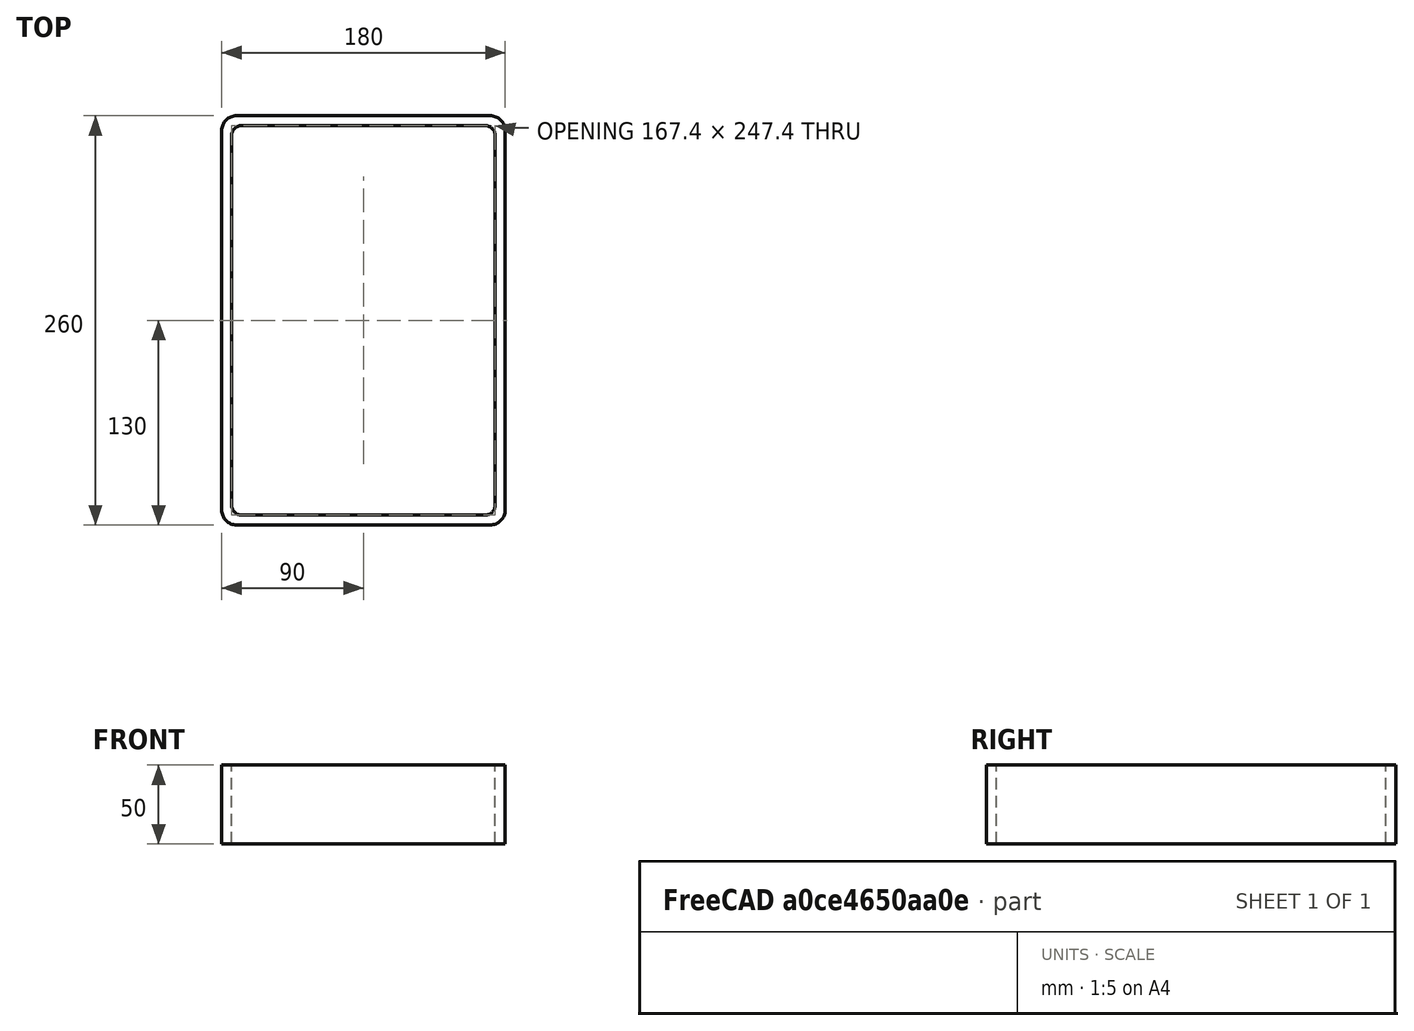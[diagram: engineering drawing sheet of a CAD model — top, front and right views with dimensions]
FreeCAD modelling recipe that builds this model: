
FCSTD DOCUMENT  (FreeCAD 0.15R4671 (Git))
Label: Rectangular hollow section 260x180x6.3 EN10219 S235JRH
License: All rights reserved
LicenseURL: http://en.wikipedia.org/wiki/All_rights_reserved
objects: Sketcher::SketchObject×1, Part::Extrusion×1
note: 2 computed .brp shape members not serialized (recipe doc carries the construction recipe); baked Part::Feature solids carry a one-line shape summary decoded from their .brp

FEATURE [Sketcher::SketchObject] Sketch
  sketch-geometry (16):
    g0: LineSegment StartX=-77.4 StartY=123.7 StartZ=0 EndX=77.4 EndY=123.7 EndZ=0
    g1: LineSegment StartX=83.7 StartY=117.4 StartZ=0 EndX=83.7 EndY=-117.4 EndZ=0
    g2: LineSegment StartX=77.4 StartY=-123.7 StartZ=0 EndX=-77.4 EndY=-123.7 EndZ=0
    g3: LineSegment StartX=-83.7 StartY=-117.4 StartZ=0 EndX=-83.7 EndY=117.4 EndZ=0
    g4: LineSegment StartX=-80.55 StartY=130 StartZ=0 EndX=80.55 EndY=130 EndZ=0
    g5: LineSegment StartX=90 StartY=120.55 StartZ=0 EndX=90 EndY=-120.55 EndZ=0
    g6: LineSegment StartX=80.55 StartY=-130 StartZ=0 EndX=-80.55 EndY=-130 EndZ=0
    g7: LineSegment StartX=-90 StartY=-120.55 StartZ=0 EndX=-90 EndY=120.55 EndZ=0
    g8: ArcOfCircle CenterX=-77.4 CenterY=117.4 CenterZ=0 NormalX=0 NormalY=0 NormalZ=1 Radius=6.3 StartAngle=1.5708 EndAngle=3.14159
    g9: ArcOfCircle CenterX=77.4 CenterY=117.4 CenterZ=0 NormalX=0 NormalY=0 NormalZ=1 Radius=6.3 StartAngle=0 EndAngle=1.5708
    g10: ArcOfCircle CenterX=77.4 CenterY=-117.4 CenterZ=0 NormalX=0 NormalY=0 NormalZ=1 Radius=6.3 StartAngle=4.71239 EndAngle=6.28319
    g11: ArcOfCircle CenterX=-77.4 CenterY=-117.4 CenterZ=0 NormalX=0 NormalY=0 NormalZ=1 Radius=6.3 StartAngle=3.14159 EndAngle=4.71239
    g12: ArcOfCircle CenterX=80.55 CenterY=120.55 CenterZ=0 NormalX=0 NormalY=0 NormalZ=1 Radius=9.45 StartAngle=0 EndAngle=1.5708
    g13: ArcOfCircle CenterX=80.55 CenterY=-120.55 CenterZ=0 NormalX=0 NormalY=0 NormalZ=1 Radius=9.45 StartAngle=4.71239 EndAngle=6.28319
    g14: ArcOfCircle CenterX=-80.55 CenterY=-120.55 CenterZ=0 NormalX=0 NormalY=0 NormalZ=1 Radius=9.45 StartAngle=3.14159 EndAngle=4.71239
    g15: ArcOfCircle CenterX=-80.55 CenterY=120.55 CenterZ=0 NormalX=0 NormalY=0 NormalZ=1 Radius=9.45 StartAngle=1.5708 EndAngle=3.14159
  constraints (36):
    c: Horizontal(g2)
    c: Vertical(g3)
    c: Horizontal(g6)
    c: Vertical(g7)
    c: Tangent(g3,g8) = 1.5708
    c: Tangent(g0,g8) = 1.5708
    c: Tangent(g0,g9) = 1.5708
    c: Tangent(g1,g9) = 1.5708
    c: Tangent(g1,g10) = 1.5708
    c: Tangent(g2,g10) = 1.5708
    c: Tangent(g2,g11) = 1.5708
    c: Tangent(g3,g11) = 1.5708
    c: Tangent(g4,g12) = 1.5708
    c: Tangent(g5,g12) = 1.5708
    c: Tangent(g5,g13) = 1.5708
    c: Tangent(g6,g13) = 1.5708
    c: Tangent(g6,g14) = 1.5708
    c: Tangent(g7,g14) = 1.5708
    c: Tangent(g7,g15) = 1.5708
    c: Tangent(g4,g15) = 1.5708
    c: Equal(g9,g8)
    c: Equal(g9,g11)
    c: Equal(g9,g10)
    c: Equal(g12,g15)
    c: Equal(g12,g14)
    c: Equal(g12,g13)
    c: Symmetric(g4,g6,g-1)
    c: Symmetric(g7,g5,g-2)
    c: DistanceY(g4,g6) = -260
    c: DistanceX(g7,g5) = 180
    c: Symmetric(g3,g1,g-2)
    c: Symmetric(g0,g2,g-1)
    c: DistanceY(g0,g4) = 6.3
    c: DistanceX(g5,g1) = -6.3
    c: Radius(g9) = 6.3
    c: Radius(g12) = 9.45
FEATURE [Part::Extrusion] Extrude  label="Rectangular hollow section 260x180x6.3 EN10219 S235JRH"
  Base = -> Sketch
  Dir = (0,0,50)
  Solid = true
